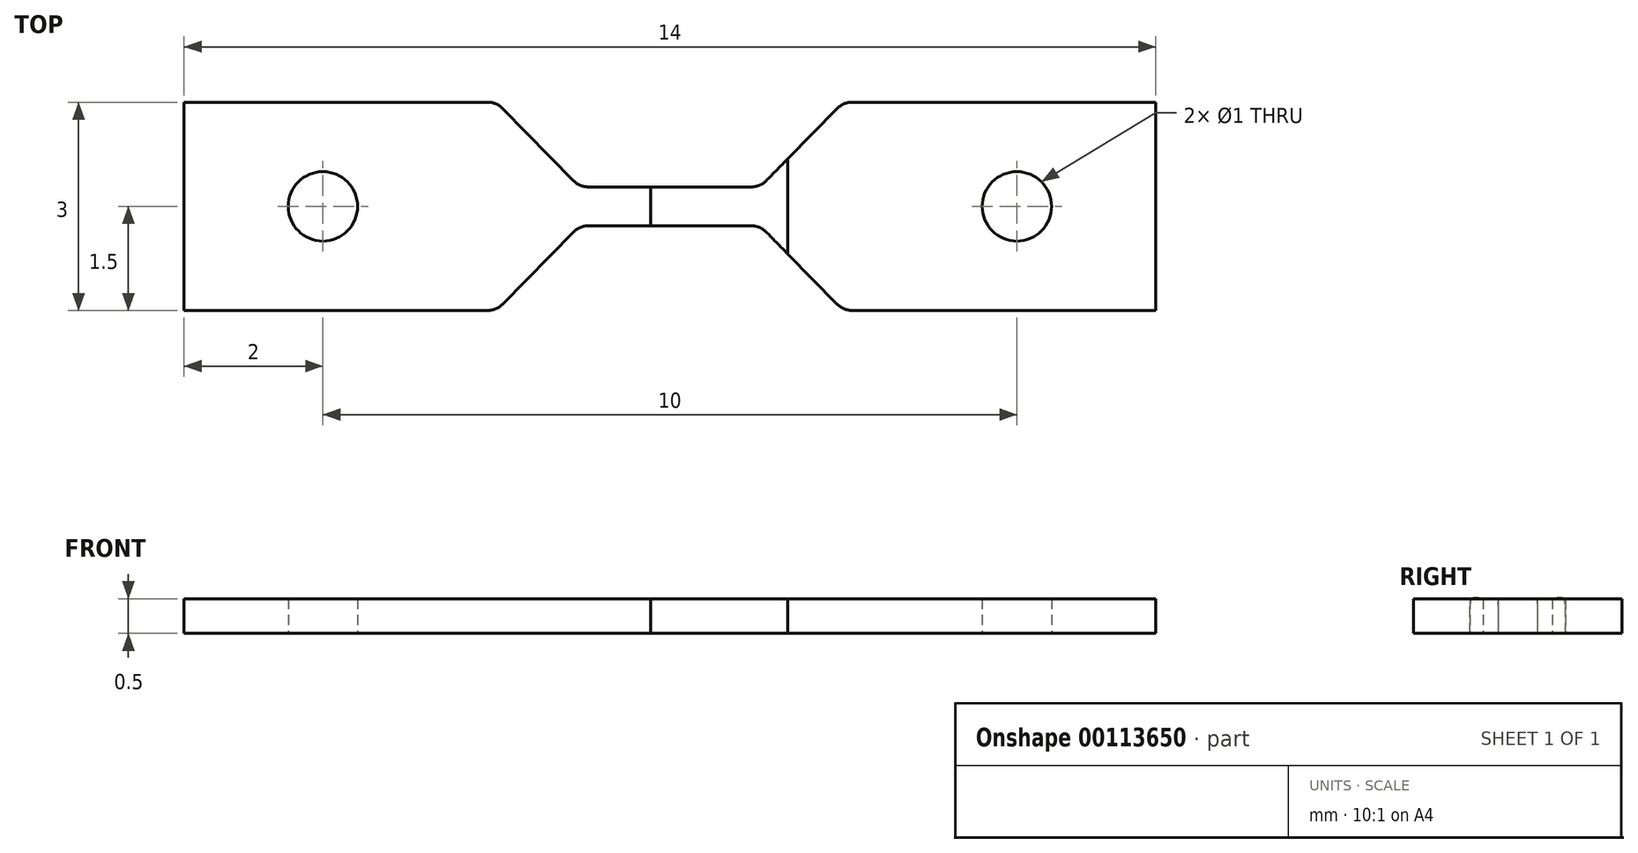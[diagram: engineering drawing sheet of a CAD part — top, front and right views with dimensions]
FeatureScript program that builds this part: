
annotation { "Feature Type Name" : "Feature", "Feature Type Description" : "" }
export const myFeature = defineFeature(function(context is Context, id is Id, definition is map)
    precondition{}
    {
        {
            var Q0;
            Q0=qCreatedBy(makeId("Top.planeOp"),FACE);
            var sketch = newSketch(context, id + "F0", { "sketchPlane" : qUnion([Q0])});
            skLineSegment(sketch, "E0", {"start": v(-7, 0) * mm, "end": v(-7, 1.5) * mm});
            skLineSegment(sketch, "E1", {"start": v(-7, 1.5) * mm, "end": v(-2.5, 1.5) * mm});
            skLineSegment(sketch, "E2", {"start": v(-2.5, 1.5) * mm, "end": v(-1.39, 0.37) * mm});
            skLineSegment(sketch, "E3", {"start": v(-1.17, 0.28) * mm, "end": v(0, 0.28) * mm});
            skPoint(sketch, "E4.visualSharp", {"position": v(-1.3, 0.28) * mm});
            skArc(sketch, "E4.filletArc", {"start": v(-1.39, 0.37) * mm, "mid": v(-1.3, 0.3) * mm, "end": v(-1.17, 0.28) * mm});
            skLineSegment(sketch, "E5.MirrorCS", {"start": v(-7, 0) * mm, "end": v(-7, -1.5) * mm});
            skLineSegment(sketch, "E6.MirrorCS", {"start": v(-7, -1.5) * mm, "end": v(-2.5, -1.5) * mm});
            skLineSegment(sketch, "E7.MirrorCS", {"start": v(-2.5, -1.5) * mm, "end": v(-1.39, -0.37) * mm});
            skLineSegment(sketch, "E8.MirrorCS", {"start": v(-1.17, -0.28) * mm, "end": v(0, -0.28) * mm});
            skArc(sketch, "E9.MirrorCS", {"start": v(-1.39, -0.37) * mm, "mid": v(-1.3, -0.3) * mm, "end": v(-1.17, -0.28) * mm});
            skCircle(sketch, "E10", {"center": v(-5, 0) * mm, "radius": 0.5 * mm});
            skArc(sketch, "E11.MirrorCS", {"start": v(1.39, -0.37) * mm, "mid": v(1.3, -0.3) * mm, "end": v(1.17, -0.28) * mm});
            skArc(sketch, "E12.MirrorCS", {"start": v(1.39, 0.37) * mm, "mid": v(1.3, 0.3) * mm, "end": v(1.17, 0.28) * mm});
            skLineSegment(sketch, "E13.MirrorCS", {"start": v(7, 0) * mm, "end": v(7, 1.5) * mm});
            skLineSegment(sketch, "E14.MirrorCS", {"start": v(7, 1.5) * mm, "end": v(2.5, 1.5) * mm});
            skLineSegment(sketch, "E15.MirrorCS", {"start": v(2.5, 1.5) * mm, "end": v(1.39, 0.37) * mm});
            skPoint(sketch, "E16.MirrorP", {"position": v(1.3, 0.28) * mm});
            skCircle(sketch, "E17.MirrorC", {"center": v(5, 0) * mm, "radius": 0.5 * mm});
            skLineSegment(sketch, "E18.MirrorCS", {"start": v(1.17, -0.28) * mm, "end": v(0, -0.28) * mm});
            skLineSegment(sketch, "E19.MirrorCS", {"start": v(2.5, -1.5) * mm, "end": v(1.39, -0.37) * mm});
            skLineSegment(sketch, "E20.MirrorCS", {"start": v(1.17, 0.28) * mm, "end": v(0, 0.28) * mm});
            skLineSegment(sketch, "E21.MirrorCS", {"start": v(7, 0) * mm, "end": v(7, -1.5) * mm});
            skLineSegment(sketch, "E22.MirrorCS", {"start": v(7, -1.5) * mm, "end": v(2.5, -1.5) * mm});
            skSolve(sketch);
        }
        {
            var Q0;
            Q0=makeQuery(id+"F0.imprint","IMPRINT",FACE,{"disambiguationData":[TD([[makeQuery(id+"F0.imprint","IMPRINT",EDGE,{"derivedFrom":sQuery(id+"F0.wireOp",EDGE,"E0")}),-1.0]])]});
            extrude(context, id + "F1", {"entities" : qUnion([Q0]), "depth" : 0.5 * mm, "offsetDistance" : 25 * mm, "symmetric" : true});
        }
        {
            var Q0;
            Q0=makeQuery(id+"F1.opExtrude","SWEPT_EDGE",EDGE,{"disambiguationData":[OSD([sQuery(id+"F0.wireOp",EDGE,"E6.MirrorCS"),sQuery(id+"F0.wireOp",EDGE,"E7.MirrorCS")])]});
            var Q1;
            Q1=makeQuery(id+"F1.opExtrude","SWEPT_EDGE",EDGE,{"disambiguationData":[OSD([sQuery(id+"F0.wireOp",EDGE,"E19.MirrorCS"),sQuery(id+"F0.wireOp",EDGE,"E22.MirrorCS")])]});
            var Q2;
            Q2=makeQuery(id+"F1.opExtrude","SWEPT_EDGE",EDGE,{"disambiguationData":[OSD([sQuery(id+"F0.wireOp",EDGE,"E1"),sQuery(id+"F0.wireOp",EDGE,"E2")])]});
            var Q3;
            Q3=makeQuery(id+"F1.opExtrude","SWEPT_EDGE",EDGE,{"disambiguationData":[OSD([sQuery(id+"F0.wireOp",EDGE,"E14.MirrorCS"),sQuery(id+"F0.wireOp",EDGE,"E15.MirrorCS")])]});
            fillet(context, id + "F2", {"entities" : qUnion([Q0, Q1, Q2, Q3]), "radius" : 0.3 * mm, "tangentPropagation" : true, "allowEdgeOverflow" : false});
        }
        {
            var Q0;
            Q0=qCreatedBy(makeId("Top.planeOp"),FACE);
            var sketch = newSketch(context, id + "F3", { "sketchPlane" : qUnion([Q0])});
            skLineSegment(sketch, "E23.bottom", {"start": v(-0.28, -1.5) * mm, "end": v(1.7, -1.5) * mm});
            skLineSegment(sketch, "E23.top", {"start": v(-0.28, 1.5) * mm, "end": v(1.7, 1.5) * mm});
            skLineSegment(sketch, "E23.left", {"start": v(-0.28, -1.5) * mm, "end": v(-0.28, 1.5) * mm});
            skLineSegment(sketch, "E23.right", {"start": v(1.7, -1.5) * mm, "end": v(1.7, 1.5) * mm});
            skSolve(sketch);
        }
        {
            var Q0;
            Q0=makeQuery(id+"F3.imprint","IMPRINT",FACE,{"disambiguationData":[TD([[makeQuery(id+"F3.imprint","IMPRINT",EDGE,{"derivedFrom":sQuery(id+"F3.wireOp",EDGE,"E23.bottom")}),1.0]])]});
            extrude(context, id + "F4", {"entities" : qUnion([Q0]), "depth" : 1 * mm, "offsetDistance" : 25 * mm, "symmetric" : true});
        }
        {
            var Q0;
            Q0=makeQuery(id+"F4.opExtrude","SWEPT_BODY",BODY,{"disambiguationData":[OSD([sQuery(id+"F3.wireOp",EDGE,"E23.bottom"),sQuery(id+"F3.wireOp",EDGE,"E23.top"),sQuery(id+"F3.wireOp",EDGE,"E23.right"),sQuery(id+"F3.wireOp",EDGE,"E23.left")])]});
            var Q1;
            Q1=makeQuery(id+"F1.opExtrude","SWEPT_BODY",BODY,{"disambiguationData":[OSD([sQuery(id+"F0.wireOp",EDGE,"E0"),sQuery(id+"F0.wireOp",EDGE,"E1"),sQuery(id+"F0.wireOp",EDGE,"E2"),sQuery(id+"F0.wireOp",EDGE,"E3"),sQuery(id+"F0.wireOp",EDGE,"E4.filletArc"),sQuery(id+"F0.wireOp",EDGE,"E5.MirrorCS"),sQuery(id+"F0.wireOp",EDGE,"E6.MirrorCS"),sQuery(id+"F0.wireOp",EDGE,"E7.MirrorCS"),sQuery(id+"F0.wireOp",EDGE,"E8.MirrorCS"),sQuery(id+"F0.wireOp",EDGE,"E9.MirrorCS"),sQuery(id+"F0.wireOp",EDGE,"E10"),sQuery(id+"F0.wireOp",EDGE,"E11.MirrorCS"),sQuery(id+"F0.wireOp",EDGE,"E12.MirrorCS"),sQuery(id+"F0.wireOp",EDGE,"E13.MirrorCS"),sQuery(id+"F0.wireOp",EDGE,"E14.MirrorCS"),sQuery(id+"F0.wireOp",EDGE,"E15.MirrorCS"),sQuery(id+"F0.wireOp",EDGE,"E17.MirrorC"),sQuery(id+"F0.wireOp",EDGE,"E18.MirrorCS"),sQuery(id+"F0.wireOp",EDGE,"E19.MirrorCS"),sQuery(id+"F0.wireOp",EDGE,"E20.MirrorCS"),sQuery(id+"F0.wireOp",EDGE,"E21.MirrorCS"),sQuery(id+"F0.wireOp",EDGE,"E22.MirrorCS")])]});
            booleanBodies(context, id + "F5", {"operationType" : BooleanOperationType.INTERSECTION, "tools" : qUnion([Q0, Q1]), "keepTools" : true});
        }
        {
            var Q0;
            Q0=makeQuery(id+"F4.opExtrude","SWEPT_BODY",BODY,{"disambiguationData":[OSD([sQuery(id+"F3.wireOp",EDGE,"E23.bottom"),sQuery(id+"F3.wireOp",EDGE,"E23.top"),sQuery(id+"F3.wireOp",EDGE,"E23.right"),sQuery(id+"F3.wireOp",EDGE,"E23.left")])]});
            var Q1;
            Q1=makeQuery(id+"F1.opExtrude","SWEPT_BODY",BODY,{"disambiguationData":[OSD([sQuery(id+"F0.wireOp",EDGE,"E0"),sQuery(id+"F0.wireOp",EDGE,"E1"),sQuery(id+"F0.wireOp",EDGE,"E2"),sQuery(id+"F0.wireOp",EDGE,"E3"),sQuery(id+"F0.wireOp",EDGE,"E4.filletArc"),sQuery(id+"F0.wireOp",EDGE,"E5.MirrorCS"),sQuery(id+"F0.wireOp",EDGE,"E6.MirrorCS"),sQuery(id+"F0.wireOp",EDGE,"E7.MirrorCS"),sQuery(id+"F0.wireOp",EDGE,"E8.MirrorCS"),sQuery(id+"F0.wireOp",EDGE,"E9.MirrorCS"),sQuery(id+"F0.wireOp",EDGE,"E10"),sQuery(id+"F0.wireOp",EDGE,"E11.MirrorCS"),sQuery(id+"F0.wireOp",EDGE,"E12.MirrorCS"),sQuery(id+"F0.wireOp",EDGE,"E13.MirrorCS"),sQuery(id+"F0.wireOp",EDGE,"E14.MirrorCS"),sQuery(id+"F0.wireOp",EDGE,"E15.MirrorCS"),sQuery(id+"F0.wireOp",EDGE,"E17.MirrorC"),sQuery(id+"F0.wireOp",EDGE,"E18.MirrorCS"),sQuery(id+"F0.wireOp",EDGE,"E19.MirrorCS"),sQuery(id+"F0.wireOp",EDGE,"E20.MirrorCS"),sQuery(id+"F0.wireOp",EDGE,"E21.MirrorCS"),sQuery(id+"F0.wireOp",EDGE,"E22.MirrorCS")])]});
            booleanBodies(context, id + "F6", {"operationType" : BooleanOperationType.SUBTRACTION, "tools" : qUnion([Q0]), "targets" : qUnion([Q1])});
        }
        {
            var Q0;
            Q0=makeQuery(id+"F5.opBoolean","COPY",EDGE,{"derivedFrom":makeQuery(id+"F1.opExtrude","CAP_EDGE",EDGE,{"disambiguationData":[OSD([sQuery(id+"F0.wireOp",EDGE,"E8.MirrorCS"),sQuery(id+"F0.wireOp",EDGE,"E18.MirrorCS")])],"isStart":false})});
            var Q1;
            Q1=makeQuery(id+"F5.opBoolean","COPY",EDGE,{"derivedFrom":makeQuery(id+"F1.opExtrude","CAP_EDGE",EDGE,{"disambiguationData":[OSD([sQuery(id+"F0.wireOp",EDGE,"E3"),sQuery(id+"F0.wireOp",EDGE,"E20.MirrorCS")])],"isStart":false})});
            fillet(context, id + "F7", {"entities" : qUnion([Q0, Q1]), "radius" : 0.1 * mm, "tangentPropagation" : true, "rho" : 0.8, "crossSection" : FilletCrossSection.CONIC, "allowEdgeOverflow" : false});
        }
    });
